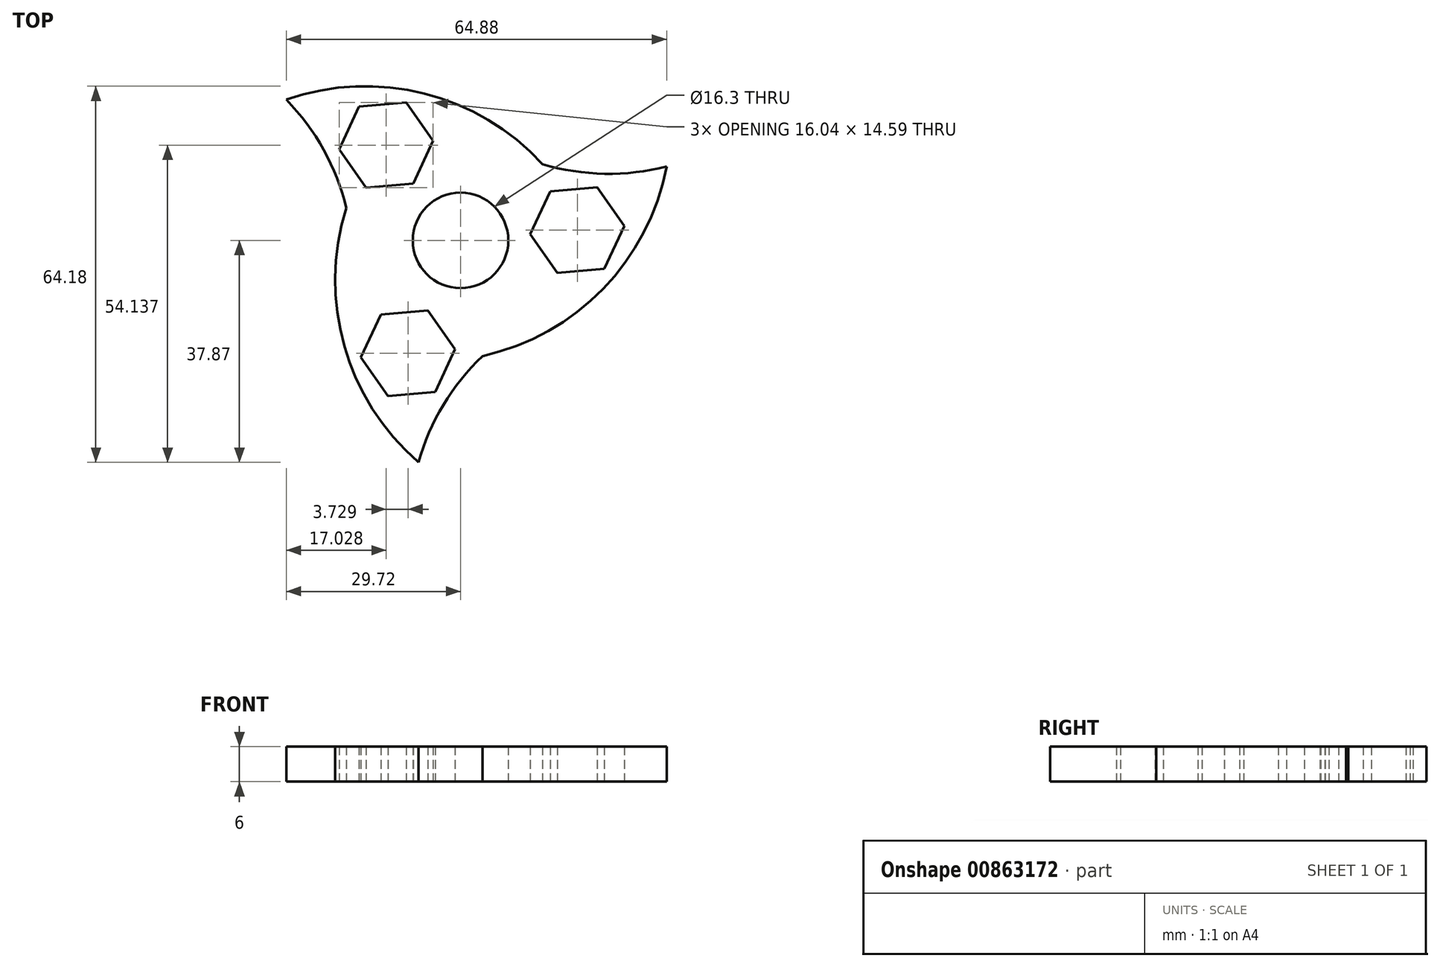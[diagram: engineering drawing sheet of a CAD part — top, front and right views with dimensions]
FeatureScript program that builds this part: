
annotation { "Feature Type Name" : "Feature", "Feature Type Description" : "" }
export const myFeature = defineFeature(function(context is Context, id is Id, definition is map)
    precondition{}
    {
        {
            var Q0;
            Q0=qCreatedBy(makeId("Top.planeOp"),FACE);
            var sketch = newSketch(context, id + "F0", { "sketchPlane" : qUnion([Q0])});
            skCircle(sketch, "E0", {"center": v(0, 0) * mm, "radius": 8.15 * mm});
            skPoint(sketch, "E1", {"position": v(0, 20.39) * mm});
            skPoint(sketch, "E2.MirrorP", {"position": v(0, -20.39) * mm});
            skArc(sketch, "E3", {"start": v(14, 13) * mm, "mid": v(24.55, 11.38) * mm, "end": v(35.16, 12.6) * mm});
            skArc(sketch, "E4", {"start": v(3.75, -19.74) * mm, "mid": v(24.3, -8.27) * mm, "end": v(35.16, 12.6) * mm});
            skArc(sketch, "E5.1.0", {"start": v(-19.48, 5.5) * mm, "mid": v(-23.35, 15.46) * mm, "end": v(-29.72, 24.03) * mm});
            skArc(sketch, "E5.1.1", {"start": v(14, 13) * mm, "mid": v(-6.2, 25.07) * mm, "end": v(-29.72, 24.03) * mm});
            skArc(sketch, "E5.2.0", {"start": v(3.75, -19.74) * mm, "mid": v(-2.93, -28.07) * mm, "end": v(-7.17, -37.87) * mm});
            skArc(sketch, "E5.2.1", {"start": v(-19.48, 5.5) * mm, "mid": v(-19.83, -18.02) * mm, "end": v(-7.17, -37.87) * mm});
            skPoint(sketch, "E5.center", {"position": v(-0.58, -0.4) * mm});
            skLineSegment(sketch, "E6", {"start": v(0, 0) * mm, "end": v(19.92, 1.74) * mm, "construction": true});
            skArc(sketch, "E7.cCircle", {"start": v(26.25, 6.72) * mm, "mid": v(13.33, -2.87) * mm, "end": v(26.77, 5.98) * mm, "construction": true});
            skLineSegment(sketch, "E7.0", {"start": v(11.9, 1.04) * mm, "end": v(15.3, 8.34) * mm});
            skLineSegment(sketch, "E7.1", {"start": v(15.3, 8.34) * mm, "end": v(23.33, 9.04) * mm});
            skLineSegment(sketch, "E7.2", {"start": v(23.33, 9.04) * mm, "end": v(27.94, 2.44) * mm});
            skLineSegment(sketch, "E7.3", {"start": v(27.94, 2.44) * mm, "end": v(24.54, -4.85) * mm});
            skLineSegment(sketch, "E7.4", {"start": v(24.54, -4.85) * mm, "end": v(16.52, -5.55) * mm});
            skLineSegment(sketch, "E7.5", {"start": v(16.52, -5.55) * mm, "end": v(11.9, 1.04) * mm});
            skLineSegment(sketch, "E8.1.0", {"start": v(-16.1, 8.97) * mm, "end": v(-20.71, 15.57) * mm});
            skLineSegment(sketch, "E8.1.1", {"start": v(-20.71, 15.57) * mm, "end": v(-17.3, 22.86) * mm});
            skLineSegment(sketch, "E8.1.2", {"start": v(-17.3, 22.86) * mm, "end": v(-9.29, 23.56) * mm});
            skLineSegment(sketch, "E8.1.3", {"start": v(-9.29, 23.56) * mm, "end": v(-4.67, 16.97) * mm});
            skLineSegment(sketch, "E8.1.4", {"start": v(-4.67, 16.97) * mm, "end": v(-8.07, 9.67) * mm});
            skLineSegment(sketch, "E8.1.5", {"start": v(-8.07, 9.67) * mm, "end": v(-16.1, 8.97) * mm});
            skLineSegment(sketch, "E8.2.0", {"start": v(-0.94, -18.54) * mm, "end": v(-4.35, -25.83) * mm});
            skLineSegment(sketch, "E8.2.1", {"start": v(-4.35, -25.83) * mm, "end": v(-12.36, -26.54) * mm});
            skLineSegment(sketch, "E8.2.2", {"start": v(-12.36, -26.54) * mm, "end": v(-16.98, -19.94) * mm});
            skLineSegment(sketch, "E8.2.3", {"start": v(-16.98, -19.94) * mm, "end": v(-13.58, -12.65) * mm});
            skLineSegment(sketch, "E8.2.4", {"start": v(-13.58, -12.65) * mm, "end": v(-5.56, -11.94) * mm});
            skLineSegment(sketch, "E8.2.5", {"start": v(-5.56, -11.94) * mm, "end": v(-0.94, -18.54) * mm});
            skPoint(sketch, "E9.orphan", {"position": v(-18.17, 9.08) * mm});
            skPoint(sketch, "E10.orphan", {"position": v(17.15, -11.3) * mm});
            skPoint(sketch, "E11.orphan", {"position": v(-18.88, -10.3) * mm});
            skPoint(sketch, "E12.orphan", {"position": v(16.44, 10.08) * mm});
            skLineSegment(sketch, "E13.2.0", {"start": v(27.94, 2.46) * mm, "end": v(25.05, -3.74) * mm});
            skPoint(sketch, "E14", {"position": v(-11.3, 16.7) * mm});
            skPoint(sketch, "E15", {"position": v(-8.3, -18.1) * mm});
            skLineSegment(sketch, "E16", {"start": v(-0.58, -0.4) * mm, "end": v(-29.72, 24.03) * mm, "construction": true});
            skLineSegment(sketch, "E17", {"start": v(-0.58, -0.4) * mm, "end": v(35.16, 12.6) * mm, "construction": true});
            skLineSegment(sketch, "E18", {"start": v(-0.58, -0.4) * mm, "end": v(-7.17, -37.87) * mm, "construction": true});
            skPoint(sketch, "E19.orphan", {"position": v(29.16, 2.56) * mm});
            skPoint(sketch, "E20.orphan", {"position": v(28.45, 3.56) * mm});
            skSolve(sketch);
        }
        {
            var Q0;
            Q0=makeQuery(id+"F0.imprint","IMPRINT",FACE,{"disambiguationData":[TD([[makeQuery(id+"F0.imprint","IMPRINT",EDGE,{"derivedFrom":sQuery(id+"F0.wireOp",EDGE,"E0")}),-1.0]])]});
            extrude(context, id + "F1", {"entities" : qUnion([Q0]), "depth" : 6 * mm, "offsetDistance" : 25 * mm});
        }
    });
